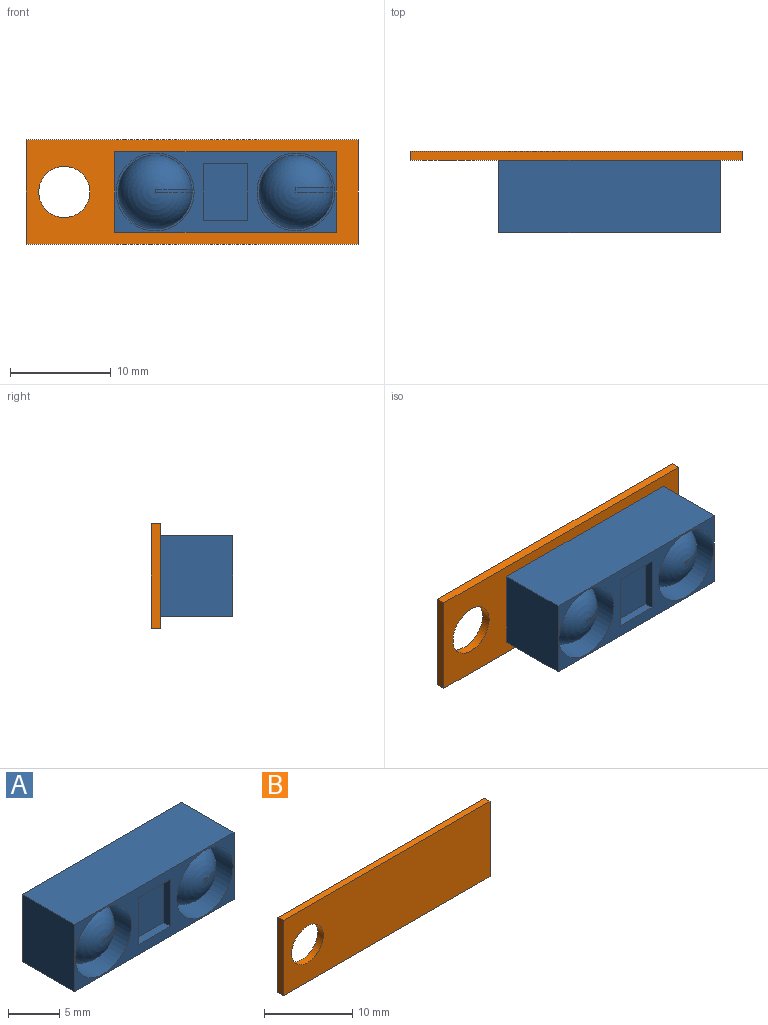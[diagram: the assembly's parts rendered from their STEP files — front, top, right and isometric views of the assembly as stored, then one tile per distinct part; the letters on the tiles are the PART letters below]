
ASSEMBLY  parts=2 mates=1
PART A: 30 faces, bbox 22x7.2x8 mm
  f0: plane 3.67x3.67mm, normal (0,0,1), area 0mm2, adj f25,f26,f27,f28,f29
  f1: plane 7.35x7.35mm, normal (0,-1,0), area 0.6mm2, adj f13,f19,f21,f23
  f2: plane 22x8mm, normal (0,-1,0), area 56.9mm2, adj f3,f4,f5,f6,f8,f9,f10,f11
  f3: plane 22x7.2mm, normal (0,0,-1), area 158.4mm2, adj f2,f4,f6,f7
  f4: plane 8x7.2mm, normal (1,0,0), area 57.6mm2, adj f2,f3,f5,f7
  f5: plane 22x7.2mm, normal (0,0,1), area 158.4mm2, adj f2,f4,f6,f7
  f6: plane 8x7.2mm, normal (-1,0,0), area 57.6mm2, adj f2,f3,f5,f7
  f7: plane 22x8mm, normal (0,1,0), area 176mm2, adj f3,f4,f5,f6
  f8: plane 4.44x0.9mm, normal (0,0,1), area 4mm2, adj f2,f9,f11,f12
  f9: plane 5.59x0.9mm, normal (-1,0,0), area 5mm2, adj f2,f8,f10,f12
  f10: plane 4.44x0.9mm, normal (0,0,-1), area 4mm2, adj f2,f9,f11,f12
  f11: plane 5.59x0.9mm, normal (1,0,0), area 5mm2, adj f2,f8,f10,f12
  f12: plane 5.59x4.44mm, normal (0,-1,0), area 24.8mm2, adj f8,f9,f10,f11
  f13: cylinder r=3.67mm len=7.35mm, axis (0,-1,0), area 53.7mm2, adj f1,f15
  f14: cylinder r=3.87mm len=7.75mm, axis (0,-1,0), area 146mm2, adj f2,f15
  f15: plane 7.75x7.75mm, normal (0,-1,0), area 4.7mm2, adj f13,f14
  f16: cylinder r=3.67mm len=7.35mm, axis (0,-1,0), area 53.7mm2, adj f18,f26,f28
  f17: cylinder r=3.87mm len=7.75mm, axis (0,-1,0), area 146mm2, adj f2,f18
  f18: plane 7.75x7.75mm, normal (0,-1,0), area 4.7mm2, adj f16,f17
  f19: plane 3.67x3.65mm, normal (0,0,1), area 0.1mm2, adj f1,f20,f21,f22,f23,f24
  f20: plane 0.44x0.03mm, normal (-1,0,0), area 0mm2, adj f19,f22,f24
  f21: plane 0.44x0.43mm, normal (1,0,0), area 0.2mm2, adj f1,f19,f23,f24
  f22: sphere r=3.67mm, area 72.4mm2, adj f19,f20,f23,f24
  f23: cylinder r=3.65mm len=7.29mm, axis (0,-1,0), area 9.8mm2, adj f1,f19,f21,f22
  f24: cylinder r=3.67mm len=3.65mm, axis (0,0,-1), area 2.3mm2, adj f19,f20,f21,f22
  f25: plane 0.2x0.01mm, normal (-1,0,0), area 0mm2, adj f0,f27,f29
  f26: plane 0.21x0.21mm, normal (1,0,0), area 0mm2, adj f0,f16,f28,f29
  f27: sphere r=3.67mm, area 79mm2, adj f0,f25,f28,f29
  f28: cylinder r=3.67mm len=7.34mm, axis (0,-1,0), area 4.5mm2, adj f0,f16,f26,f27
  f29: cylinder r=3.67mm len=3.67mm, axis (0,0,-1), area 1.1mm2, adj f0,f25,f26,f27
PART B: 7 faces, bbox 33x0.9x10.4 mm
  f0: plane 33.02x0.9mm, normal (0,0,1), area 29.7mm2, adj f1,f4,f5,f6
  f1: plane 10.41x0.9mm, normal (-1,0,0), area 9.4mm2, adj f0,f2,f5,f6
  f2: plane 33.02x0.9mm, normal (0,0,-1), area 29.7mm2, adj f1,f4,f5,f6
  f3: cylinder r=2.54mm len=5.08mm, axis (0,1,0), area 14.4mm2, adj f5,f6
  f4: plane 10.41x0.9mm, normal (1,0,0), area 9.4mm2, adj f0,f2,f5,f6
  f5: plane 33.02x10.41mm, normal (0,-1,0), area 323.6mm2, adj f0,f1,f2,f3,f4
  f6: plane 33.02x10.41mm, normal (0,1,0), area 323.6mm2, adj f0,f1,f2,f3,f4
PLACE A t=(11.58,6.82,3.77)mm
PLACE B t=(-8.26,7.72,-1.44)mm
MATE parallel A.f7 <-> B.f5  axis (0,1,0) through (11.58,6.82,3.77)mm
